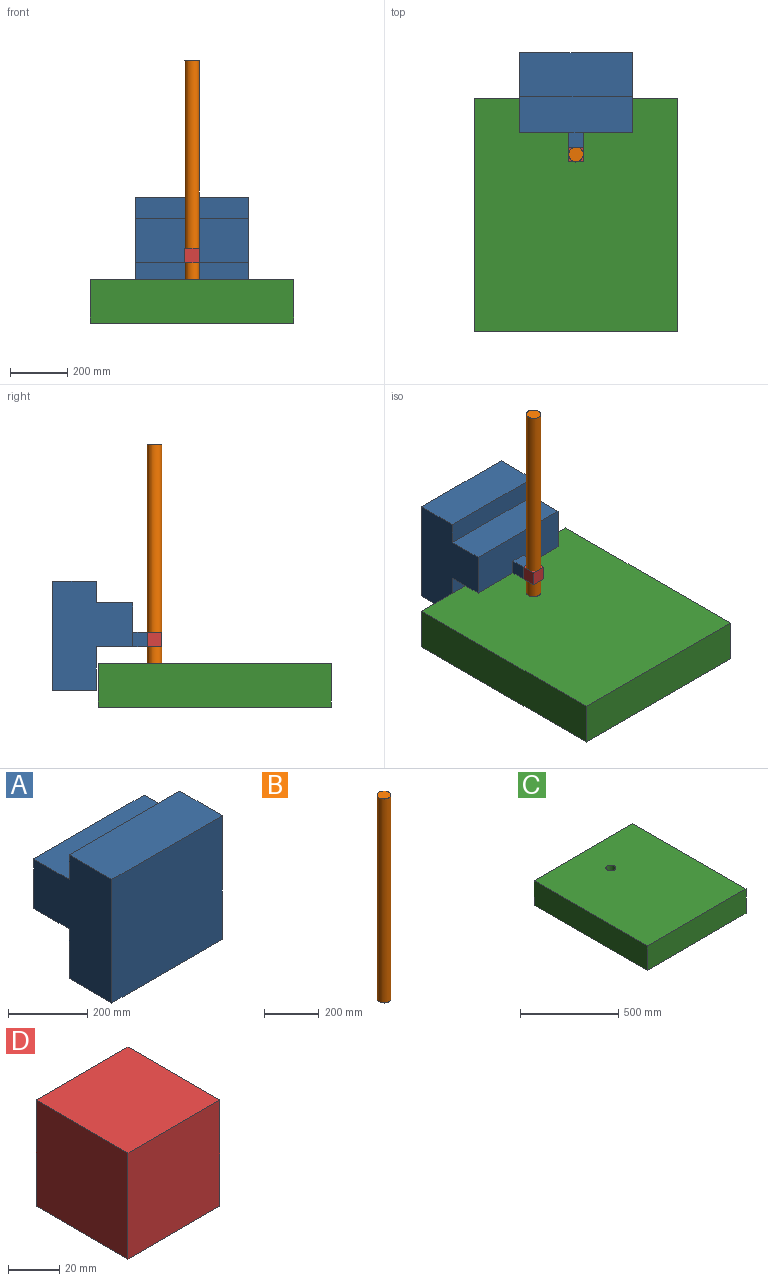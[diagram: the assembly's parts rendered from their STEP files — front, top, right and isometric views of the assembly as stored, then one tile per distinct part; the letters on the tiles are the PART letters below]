
ASSEMBLY  parts=4 mates=3
PART A: 14 faces, bbox 393.7x330.2x381 mm
  f0: plane 50.8x50.8mm, normal (1,0,0), area 2580.6mm2, adj f1,f3,f4,f5
  f1: plane 50.8x50.8mm, normal (0,1,0), area 2580.6mm2, adj f0,f2,f3,f4
  f2: plane 50.8x50.8mm, normal (-1,0,0), area 2580.6mm2, adj f1,f3,f4,f5
  f3: plane 393.7x177.8mm, normal (0,0,-1), area 52580.5mm2, adj f0,f1,f2,f5,f6,f7,f9
  f4: plane 50.8x50.8mm, normal (0,0,1), area 2580.6mm2, adj f0,f1,f2,f5
  f5: plane 393.7x152.4mm, normal (0,1,0), area 57419.2mm2, adj f0,f2,f3,f4,f6,f7,f8
  f6: plane 381x279.4mm, normal (-1,0,0), area 77419.2mm2, adj f3,f5,f8,f9,f10,f11,f12,f13
  f7: plane 381x279.4mm, normal (1,0,0), area 77419.2mm2, adj f3,f5,f8,f9,f10,f11,f12,f13
  f8: plane 393.7x127mm, normal (0,0,1), area 49999.9mm2, adj f5,f6,f7,f10
  f9: plane 393.7x152.4mm, normal (0,1,0), area 59999.9mm2, adj f3,f6,f7,f12
  f10: plane 393.7x76.2mm, normal (0,1,0), area 29999.9mm2, adj f6,f7,f8,f13
  f11: plane 393.7x381mm, normal (0,-1,0), area 149999.7mm2, adj f6,f7,f12,f13
  f12: plane 393.7x152.4mm, normal (0,0,-1), area 59999.9mm2, adj f6,f7,f9,f11
  f13: plane 393.7x152.4mm, normal (0,0,1), area 59999.9mm2, adj f6,f7,f10,f11
PART B: 3 faces, bbox 50.8x50.8x914.4 mm
  f0: cylinder r=25.4mm len=914.4mm, axis (0,0,-1), area 145931.8mm2, adj f1,f2
  f1: plane 50.8x50.8mm, normal (0,0,1), area 2026.8mm2, adj f0
  f2: plane 50.8x50.8mm, normal (0,0,-1), area 2026.8mm2, adj f0
PART C: 7 faces, bbox 711.2x812.8x152.4 mm
  f0: plane 812.8x152.4mm, normal (1,0,0), area 123870.7mm2, adj f1,f3,f5,f6
  f1: plane 711.2x152.4mm, normal (0,1,0), area 108386.9mm2, adj f0,f2,f5,f6
  f2: plane 812.8x152.4mm, normal (-1,0,0), area 123870.7mm2, adj f1,f3,f5,f6
  f3: plane 711.2x152.4mm, normal (0,-1,0), area 108386.9mm2, adj f0,f2,f5,f6
  f4: cylinder r=25.4mm len=152.4mm, axis (0,0,-1), area 24322mm2, adj f5,f6
  f5: plane 812.8x711.2mm, normal (0,0,1), area 576036.5mm2, adj f0,f1,f2,f3,f4
  f6: plane 812.8x711.2mm, normal (0,0,-1), area 576036.5mm2, adj f0,f1,f2,f3,f4
PART D: 6 faces, bbox 50.8x50.8x50.8 mm
  f0: plane 50.8x50.8mm, normal (0,-1,0), area 2580.6mm2, adj f1,f3,f4,f5
  f1: plane 50.8x50.8mm, normal (1,0,0), area 2580.6mm2, adj f0,f2,f4,f5
  f2: plane 50.8x50.8mm, normal (0,1,0), area 2580.6mm2, adj f1,f3,f4,f5
  f3: plane 50.8x50.8mm, normal (-1,0,0), area 2580.6mm2, adj f0,f2,f4,f5
  f4: plane 50.8x50.8mm, normal (0,0,-1), area 2580.6mm2, adj f0,f1,f2,f3
  f5: plane 50.8x50.8mm, normal (0,0,1), area 2580.6mm2, adj f0,f1,f2,f3
PLACE A rot(axis=(0,0,1),180deg) t=(-96.54,358.83,-60.31)mm
PLACE B t=(-96.6,34.41,-321.93)mm
PLACE C t=(-96.6,34.41,-321.93)mm fixed
PLACE D rot(axis=(0,0,1),180deg) t=(-96.54,358.83,-60.31)mm
MATE cylindrical D.f5 <-> B.f0  axis (0,0,1) through (-96.6,243.96,-60.31)mm
MATE fastened A.f1 <-> D.f0  axis (0,-1,0) through (-96.58,269.36,-85.71)mm
MATE fastened C.f4 <-> B.f0  axis (0,0,-1) through (-96.6,243.96,-321.93)mm
